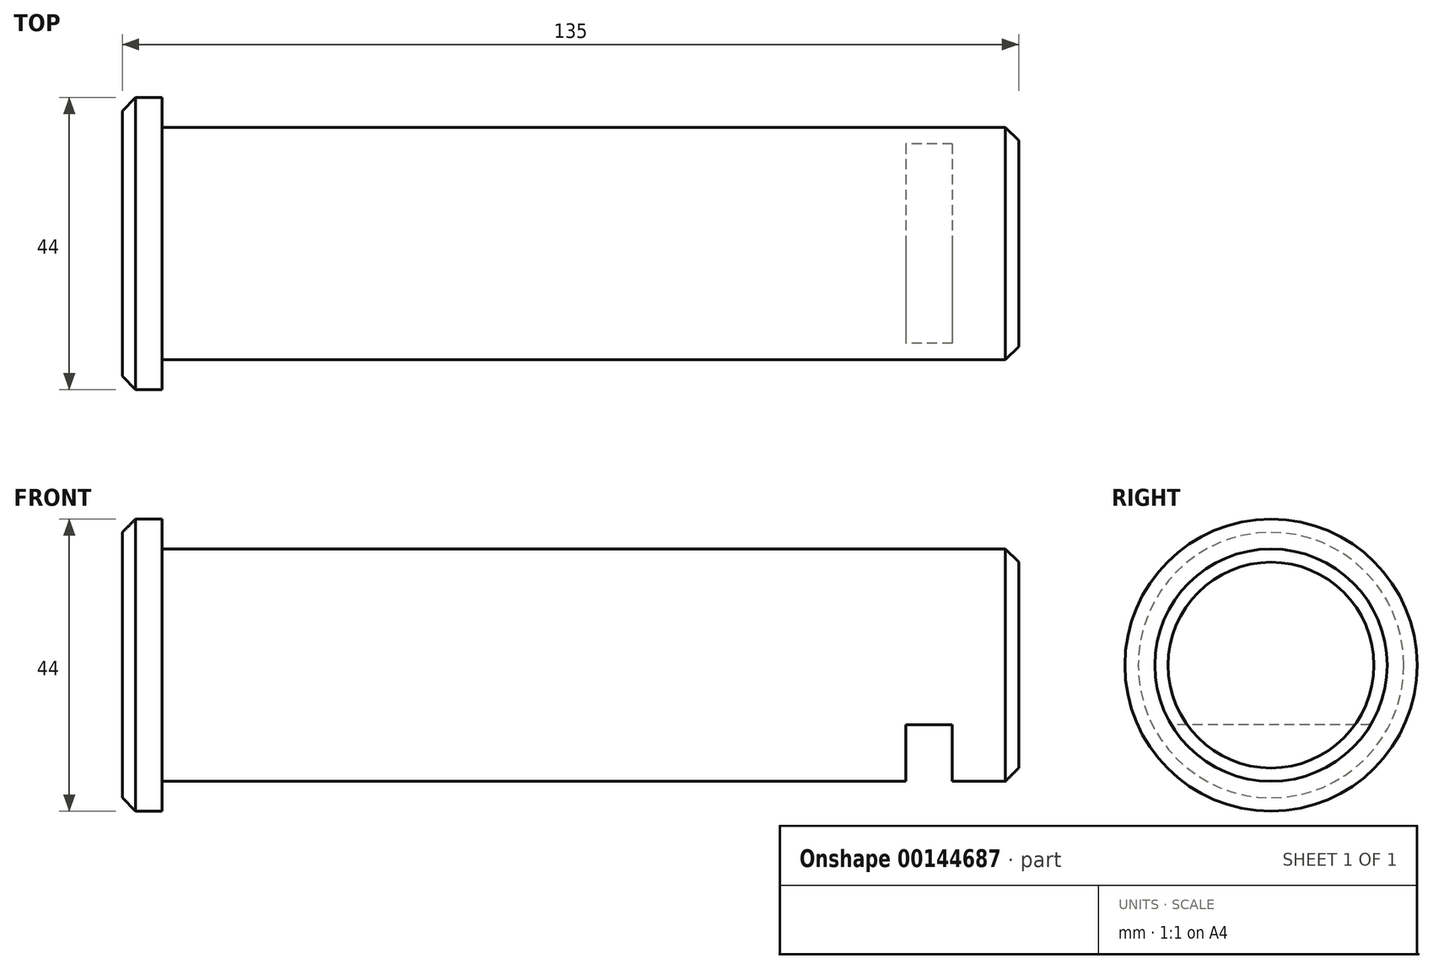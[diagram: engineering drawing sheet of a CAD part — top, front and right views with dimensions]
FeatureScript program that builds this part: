
annotation { "Feature Type Name" : "Feature", "Feature Type Description" : "" }
export const myFeature = defineFeature(function(context is Context, id is Id, definition is map)
    precondition{}
    {
        {
            var Q0;
            Q0=qCreatedBy(makeId("Right.planeOp"),FACE);
            var sketch = newSketch(context, id + "F0", { "sketchPlane" : qUnion([Q0])});
            skCircle(sketch, "E0", {"center": v(0, 0) * mm, "radius": 17.5 * mm});
            skSolve(sketch);
        }
        {
            var Q0;
            Q0 = qSketchRegion(id + "F0", true);
            extrude(context, id + "F1", {"entities" : qUnion([Q0]), "depth" : 129 * mm});
        }
        {
            var Q0;
            Q0=makeQuery(id+"F1.opExtrude","CAP_FACE",FACE,{"disambiguationData":[OSD([sQuery(id+"F0.wireOp",EDGE,"E0")])],"isStart":false});
            chamfer(context, id + "F2", {"entities" : qUnion([Q0]), "width" : 2 * mm, "tangentPropagation" : true});
        }
        {
            var Q0;
            Q0=makeQuery(id+"F1.opExtrude","CAP_FACE",FACE,{"disambiguationData":[OSD([sQuery(id+"F0.wireOp",EDGE,"E0")])],"isStart":true});
            var sketch = newSketch(context, id + "F3", { "sketchPlane" : qUnion([Q0])});
            skCircle(sketch, "E1", {"center": v(0, 0) * mm, "radius": 22 * mm});
            skSolve(sketch);
        }
        {
            var Q0;
            Q0 = qSketchRegion(id + "F3", true);
            extrude(context, id + "F4", {"entities" : qUnion([Q0]), "operationType" : NewBodyOperationType.ADD, "depth" : 6 * mm});
        }
        {
            var Q0;
            Q0=makeQuery(id+"F4.opExtrude","CAP_EDGE",EDGE,{"disambiguationData":[OSD([sQuery(id+"F3.wireOp",EDGE,"E1")])],"isStart":false});
            chamfer(context, id + "F5", {"entities" : qUnion([Q0]), "width" : 2 * mm, "tangentPropagation" : true});
        }
        {
            var Q0;
            Q0=qCreatedBy(makeId("Front.planeOp"),FACE);
            var sketch = newSketch(context, id + "F6", { "sketchPlane" : qUnion([Q0])});
            skLineSegment(sketch, "E2", {"start": v(0, 17.5) * mm, "end": v(127, 17.5) * mm, "construction": true});
            skLineSegment(sketch, "E3", {"start": v(127, -17.5) * mm, "end": v(0, -17.5) * mm, "construction": true});
            skLineSegment(sketch, "E4.0", {"start": v(0, -22) * mm, "end": v(0, 22) * mm, "construction": true});
            skLineSegment(sketch, "E5.0", {"start": v(112, -22) * mm, "end": v(112, 22) * mm, "construction": true});
            skLineSegment(sketch, "E6.0", {"start": v(0, -9) * mm, "end": v(127, -9) * mm, "construction": true});
            skLineSegment(sketch, "E7.bottom", {"start": v(112, -9) * mm, "end": v(119, -9) * mm});
            skLineSegment(sketch, "E7.top", {"start": v(112, -26.9) * mm, "end": v(119, -26.9) * mm});
            skLineSegment(sketch, "E7.left", {"start": v(112, -9) * mm, "end": v(112, -26.9) * mm});
            skLineSegment(sketch, "E7.right", {"start": v(119, -9) * mm, "end": v(119, -26.9) * mm});
            skSolve(sketch);
        }
        {
            var Q0;
            Q0 = qSketchRegion(id + "F6", true);
            extrude(context, id + "F7", {"entities" : qUnion([Q0]), "operationType" : NewBodyOperationType.REMOVE, "endBound" : BoundingType.SYMMETRIC, "oppositeDirection" : true, "depth" : 50 * mm});
        }
    });
